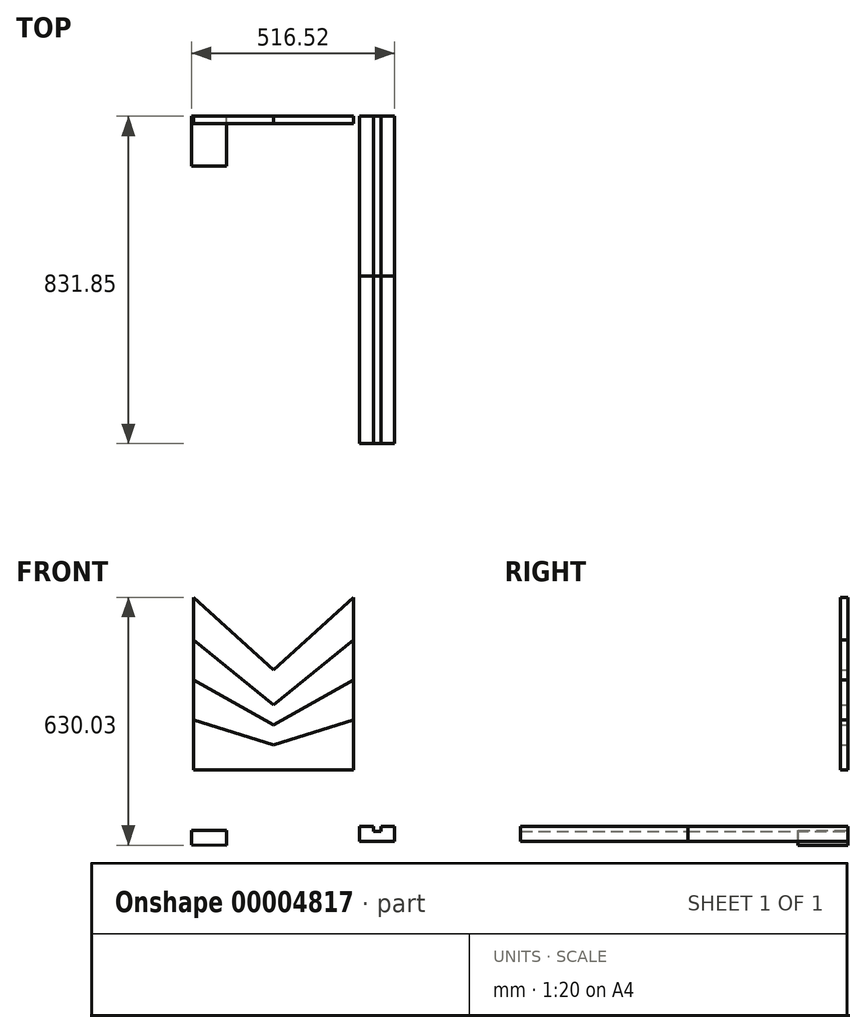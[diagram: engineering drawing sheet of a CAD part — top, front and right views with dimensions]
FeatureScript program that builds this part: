
annotation { "Feature Type Name" : "Feature", "Feature Type Description" : "" }
export const myFeature = defineFeature(function(context is Context, id is Id, definition is map)
    precondition{}
    {
        {
            var Q0;
            Q0=qCreatedBy(makeId("Front.planeOp"),FACE);
            var sketch = newSketch(context, id + "F0", { "sketchPlane" : qUnion([Q0])});
            skLineSegment(sketch, "E0.bottom", {"start": v(220.67, -99.57) * mm, "end": v(255.6, -99.57) * mm});
            skLineSegment(sketch, "E0.top", {"start": v(220.67, -137.67) * mm, "end": v(309.57, -137.67) * mm});
            skLineSegment(sketch, "E0.left", {"start": v(220.67, -99.57) * mm, "end": v(220.67, -137.67) * mm});
            skLineSegment(sketch, "E0.right", {"start": v(309.57, -99.57) * mm, "end": v(309.57, -137.67) * mm});
            skLineSegment(sketch, "E1.top", {"start": v(255.6, -112.27) * mm, "end": v(274.65, -112.27) * mm});
            skLineSegment(sketch, "E1.left", {"start": v(255.6, -99.57) * mm, "end": v(255.6, -112.27) * mm});
            skLineSegment(sketch, "E1.right", {"start": v(274.65, -99.57) * mm, "end": v(274.65, -112.27) * mm});
            skLineSegment(sketch, "E2.trimOffspring", {"start": v(274.65, -99.57) * mm, "end": v(309.57, -99.57) * mm});
            skLineSegment(sketch, "E3.bottom", {"start": v(-200.79, 171.69) * mm, "end": v(2.41, 108.19) * mm});
            skLineSegment(sketch, "E3.top", {"start": v(-200.79, 44.69) * mm, "end": v(2.41, 44.69) * mm});
            skLineSegment(sketch, "E3.left", {"start": v(-200.79, 171.69) * mm, "end": v(-200.79, 44.69) * mm});
            skLineSegment(sketch, "E3.right", {"start": v(2.41, 108.19) * mm, "end": v(2.41, 44.69) * mm});
            skLineSegment(sketch, "E4.0.MirrorCS", {"start": v(205.61, 44.69) * mm, "end": v(2.41, 44.69) * mm});
            skLineSegment(sketch, "E4.1.MirrorCS", {"start": v(205.61, 171.69) * mm, "end": v(205.61, 44.69) * mm});
            skLineSegment(sketch, "E4.2.MirrorCS", {"start": v(205.61, 171.69) * mm, "end": v(2.41, 108.19) * mm});
            skLineSegment(sketch, "E5.bottom", {"start": v(-200.79, 273.39) * mm, "end": v(2.41, 159.09) * mm});
            skLineSegment(sketch, "E5.top", {"start": v(-200.79, 44.79) * mm, "end": v(2.41, 44.79) * mm});
            skLineSegment(sketch, "E5.left", {"start": v(-200.79, 273.39) * mm, "end": v(-200.79, 44.79) * mm});
            skLineSegment(sketch, "E5.right", {"start": v(2.41, 159.09) * mm, "end": v(2.41, 44.79) * mm});
            skLineSegment(sketch, "E6.0.MirrorCS", {"start": v(205.61, 273.39) * mm, "end": v(2.41, 159.09) * mm});
            skLineSegment(sketch, "E7.0.MirrorCS", {"start": v(205.61, 273.39) * mm, "end": v(205.61, 44.79) * mm});
            skLineSegment(sketch, "E8.0.MirrorCS", {"start": v(205.61, 44.79) * mm, "end": v(2.41, 44.79) * mm});
            skLineSegment(sketch, "E9.bottom", {"start": v(-200.79, 374.99) * mm, "end": v(2.41, 209.89) * mm});
            skLineSegment(sketch, "E9.left", {"start": v(-200.79, 374.99) * mm, "end": v(-200.79, 44.79) * mm});
            skLineSegment(sketch, "E9.right", {"start": v(2.41, 209.89) * mm, "end": v(2.41, 44.79) * mm});
            skLineSegment(sketch, "E10.0.MirrorCS", {"start": v(205.61, 374.99) * mm, "end": v(2.41, 209.89) * mm});
            skLineSegment(sketch, "E11.0.MirrorCS", {"start": v(205.61, 374.99) * mm, "end": v(205.61, 44.79) * mm});
            skLineSegment(sketch, "E12.bottom", {"start": v(-200.79, 482.94) * mm, "end": v(2.41, 298.79) * mm});
            skLineSegment(sketch, "E12.left", {"start": v(-200.79, 482.94) * mm, "end": v(-200.79, 44.79) * mm});
            skLineSegment(sketch, "E12.right", {"start": v(2.41, 298.79) * mm, "end": v(2.41, 44.79) * mm});
            skLineSegment(sketch, "E13.0.MirrorCS", {"start": v(205.61, 482.94) * mm, "end": v(2.41, 298.79) * mm});
            skLineSegment(sketch, "E14.0.MirrorCS", {"start": v(205.61, 482.94) * mm, "end": v(205.61, 44.79) * mm});
            skCircle(sketch, "E15", {"center": v(0, 406.74) * mm, "radius": 76.2 * mm, "construction": true});
            skLineSegment(sketch, "E16", {"start": v(-200.79, 482.94) * mm, "end": v(205.61, 482.94) * mm});
            skCircle(sketch, "E17", {"center": v(2.41, 298.79) * mm, "radius": 177.8 * mm, "construction": true});
            skLineSegment(sketch, "E18", {"start": v(-118.05, -147.1) * mm, "end": v(-118.05, -109) * mm});
            skLineSegment(sketch, "E19", {"start": v(-118.05, -109) * mm, "end": v(-206.95, -109) * mm});
            skLineSegment(sketch, "E20", {"start": v(-206.95, -109) * mm, "end": v(-206.95, -146.74) * mm});
            skLineSegment(sketch, "E21", {"start": v(-206.95, -146.74) * mm, "end": v(-118.05, -147.1) * mm});
            skSolve(sketch);
        }
        {
            var Q0;
            Q0=makeQuery(id+"F0.imprint","IMPRINT",FACE,{"disambiguationData":[TD([[makeQuery(id+"F0.imprint","IMPRINT",EDGE,{"derivedFrom":sQuery(id+"F0.wireOp",EDGE,"E0.bottom")}),-1.0]])]});
            extrude(context, id + "F1", {"entities" : qUnion([Q0]), "depth" : 406.4 * mm});
        }
        {
            var Q0;
            Q0=makeQuery(id+"F1.opExtrude","CAP_FACE",FACE,{"disambiguationData":[OSD([sQuery(id+"F0.wireOp",EDGE,"E0.bottom"),sQuery(id+"F0.wireOp",EDGE,"E0.top"),sQuery(id+"F0.wireOp",EDGE,"E0.left"),sQuery(id+"F0.wireOp",EDGE,"E0.right"),sQuery(id+"F0.wireOp",EDGE,"E1.top"),sQuery(id+"F0.wireOp",EDGE,"E1.left"),sQuery(id+"F0.wireOp",EDGE,"E1.right"),sQuery(id+"F0.wireOp",EDGE,"E2.trimOffspring")])],"isStart":false});
            extrude(context, id + "F2", {"entities" : qUnion([Q0]), "depth" : 425.45 * mm});
        }
        {
            var Q0;
            Q0=makeQuery(id+"F0.imprint","IMPRINT",FACE,{"disambiguationData":[TD([[makeQuery(id+"F0.imprint","IMPRINT",EDGE,{"derivedFrom":sQuery(id+"F0.wireOp",EDGE,"E18")}),1.0]])]});
            extrude(context, id + "F3", {"entities" : qUnion([Q0]), "depth" : 127 * mm});
        }
        {
            var Q0;
            {var subQ2=sQuery(id+"F0.wireOp",EDGE,"E3.bottom");Q0=makeQuery(id+"F0.imprint","IMPRINT",FACE,{"disambiguationData":[TD([[makeQuery(id+"F0.imprint","IMPRINT",EDGE,{"derivedFrom":subQ2}),-1.0]])]});}
            var Q1;
            {var subQ2=sQuery(id+"F0.wireOp",EDGE,"E4.2.MirrorCS");Q1=makeQuery(id+"F0.imprint","IMPRINT",FACE,{"disambiguationData":[TD([[makeQuery(id+"F0.imprint","IMPRINT",EDGE,{"derivedFrom":subQ2}),1.0]])]});}
            extrude(context, id + "F4", {"entities" : qUnion([Q0, Q1]), "depth" : 19.05 * mm});
        }
        {
            var Q0;
            {var subQ2=sQuery(id+"F0.wireOp",EDGE,"E4.2.MirrorCS");Q0=makeQuery(id+"F0.imprint","IMPRINT",FACE,{"disambiguationData":[TD([[makeQuery(id+"F0.imprint","IMPRINT",EDGE,{"derivedFrom":subQ2}),-1.0]])]});}
            var Q1;
            {var subQ2=sQuery(id+"F0.wireOp",EDGE,"E3.bottom");Q1=makeQuery(id+"F0.imprint","IMPRINT",FACE,{"disambiguationData":[TD([[makeQuery(id+"F0.imprint","IMPRINT",EDGE,{"derivedFrom":subQ2}),1.0]])]});}
            extrude(context, id + "F5", {"entities" : qUnion([Q0, Q1]), "depth" : 19.05 * mm});
        }
        {
            var Q0;
            {var subQ2=sQuery(id+"F0.wireOp",EDGE,"E6.0.MirrorCS");Q0=makeQuery(id+"F0.imprint","IMPRINT",FACE,{"disambiguationData":[TD([[makeQuery(id+"F0.imprint","IMPRINT",EDGE,{"derivedFrom":subQ2}),-1.0]])]});}
            var Q1;
            {var subQ2=sQuery(id+"F0.wireOp",EDGE,"E5.bottom");Q1=makeQuery(id+"F0.imprint","IMPRINT",FACE,{"disambiguationData":[TD([[makeQuery(id+"F0.imprint","IMPRINT",EDGE,{"derivedFrom":subQ2}),1.0]])]});}
            extrude(context, id + "F6", {"entities" : qUnion([Q0, Q1]), "depth" : 19.05 * mm});
        }
        {
            var Q0;
            {var subQ2=sQuery(id+"F0.wireOp",EDGE,"E10.0.MirrorCS");Q0=makeQuery(id+"F0.imprint","IMPRINT",FACE,{"disambiguationData":[TD([[makeQuery(id+"F0.imprint","IMPRINT",EDGE,{"derivedFrom":subQ2}),-1.0]])]});}
            var Q1;
            {var subQ2=sQuery(id+"F0.wireOp",EDGE,"E9.bottom");Q1=makeQuery(id+"F0.imprint","IMPRINT",FACE,{"disambiguationData":[TD([[makeQuery(id+"F0.imprint","IMPRINT",EDGE,{"derivedFrom":subQ2}),1.0]])]});}
            extrude(context, id + "F7", {"entities" : qUnion([Q0, Q1]), "depth" : 19.05 * mm});
        }
    });
